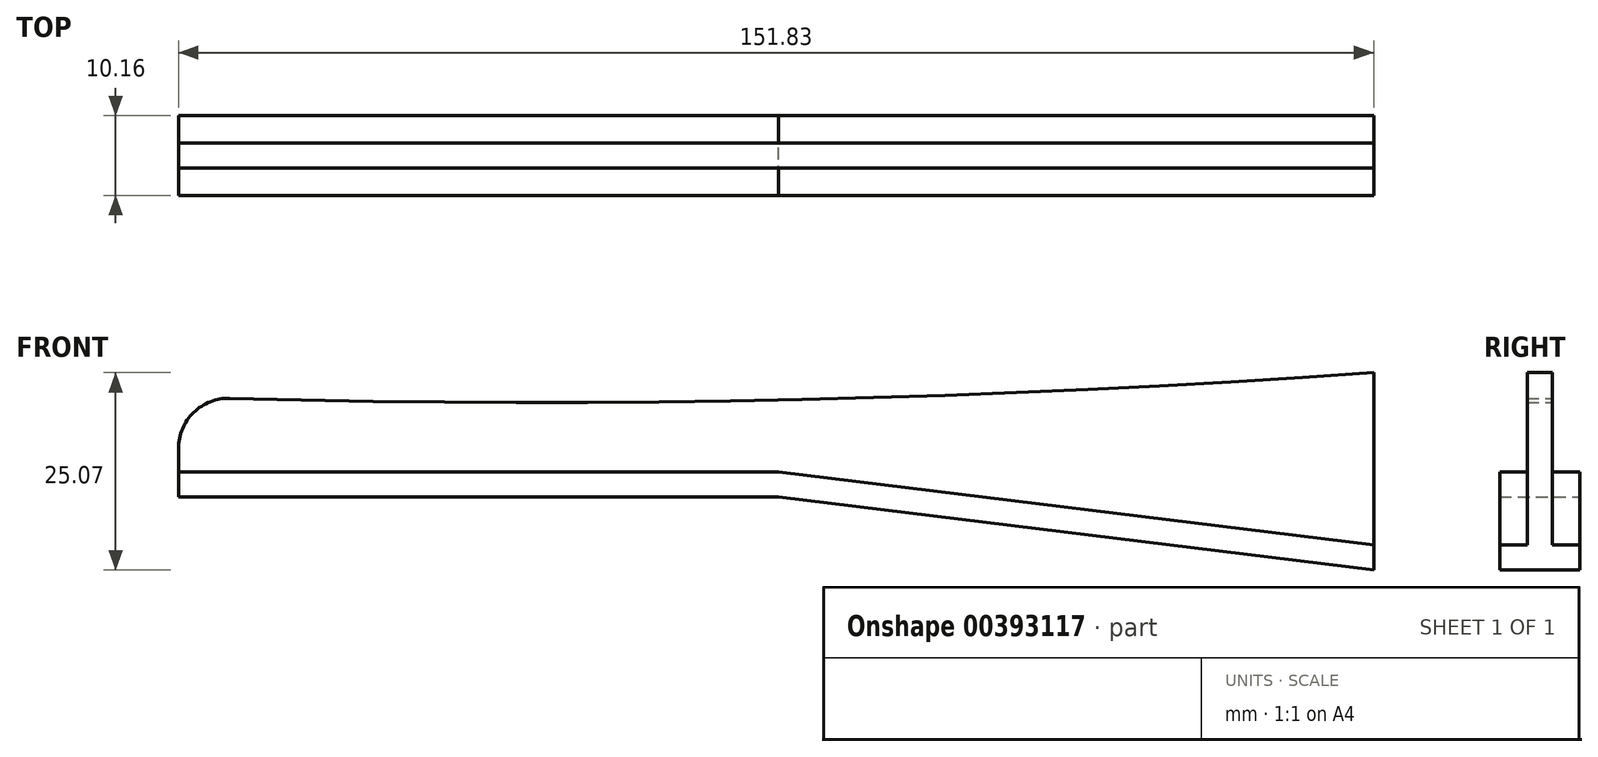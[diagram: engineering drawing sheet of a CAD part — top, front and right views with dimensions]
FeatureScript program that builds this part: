
annotation { "Feature Type Name" : "Feature", "Feature Type Description" : "" }
export const myFeature = defineFeature(function(context is Context, id is Id, definition is map)
    precondition{}
    {
        {
            var Q0;
            Q0=qCreatedBy(makeId("Front.planeOp"),FACE);
            var sketch = newSketch(context, id + "F0", { "sketchPlane" : qUnion([Q0])});
            skLineSegment(sketch, "E0.top", {"start": v(-40.64, -12.7) * mm, "end": v(35.56, -12.7) * mm});
            skLineSegment(sketch, "E0.left", {"start": v(-40.64, -6.54) * mm, "end": v(-40.64, -12.7) * mm});
            skLineSegment(sketch, "E0.right", {"start": v(35.56, -0.4) * mm, "end": v(35.56, -12.7) * mm});
            skPoint(sketch, "E0.middle", {"position": v(0, 0) * mm});
            skLineSegment(sketch, "E1", {"start": v(35.56, -12.7) * mm, "end": v(111.2, -12.7) * mm});
            skLineSegment(sketch, "E2", {"start": v(35.56, -12.7) * mm, "end": v(111.2, -21.99) * mm});
            skLineSegment(sketch, "E3", {"start": v(111.2, -21.99) * mm, "end": v(111.2, 3.08) * mm});
            skPoint(sketch, "E4", {"position": v(111.2, -12.7) * mm});
            skPoint(sketch, "E5", {"position": v(-40.64, 0) * mm});
            skPoint(sketch, "E6", {"position": v(111.2, 3.08) * mm});
            skArc(sketch, "E7", {"start": v(-34.12, -0.19) * mm, "mid": v(38.58, -0.34) * mm, "end": v(111.2, 3.08) * mm});
            skPoint(sketch, "E8", {"position": v(-40.64, -9.53) * mm});
            skPoint(sketch, "E9", {"position": v(35.56, -9.53) * mm});
            skPoint(sketch, "E9.positionSnap0", {"position": v(35.56, -6.55) * mm});
            skPoint(sketch, "E10", {"position": v(111.2, -18.81) * mm});
            skLineSegment(sketch, "E11", {"start": v(-40.64, -9.53) * mm, "end": v(35.56, -9.53) * mm});
            skLineSegment(sketch, "E12", {"start": v(35.56, -9.53) * mm, "end": v(111.2, -18.81) * mm});
            skArc(sketch, "E13.filletArc", {"start": v(-34.12, -0.19) * mm, "mid": v(-38.72, -1.99) * mm, "end": v(-40.64, -6.54) * mm});
            skSolve(sketch);
        }
        {
            var Q0;
            {var subQ0=sQuery(id+"F0.wireOp",EDGE,"E0.top");Q0=makeQuery(id+"F0.imprint","IMPRINT",FACE,{"disambiguationData":[TD([[makeQuery(id+"F0.imprint","IMPRINT",EDGE,{"derivedFrom":subQ0}),1.0]])]});}
            var Q1;
            {var subQ0=sQuery(id+"F0.wireOp",EDGE,"E2");Q1=makeQuery(id+"F0.imprint","IMPRINT",FACE,{"disambiguationData":[TD([[makeQuery(id+"F0.imprint","IMPRINT",EDGE,{"derivedFrom":subQ0}),1.0]])]});}
            var Q2;
            {var subQ0=sQuery(id+"F0.wireOp",EDGE,"E1");var subQ3=sQuery(id+"F0.wireOp",EDGE,"E12");var subQ5=makeQuery(id+"F0.imprint","INTERSECT",VERTEX,{"derivedFrom":[subQ0,subQ3]});Q2=makeQuery(id+"F0.imprint","IMPRINT",FACE,{"disambiguationData":[TD([[makeQuery(id+"F0.imprint","IMPRINT",EDGE,{"disambiguationData":[TD([[subQ5,1.0]])],"derivedFrom":subQ3}),-1.0]])]});}
            extrude(context, id + "F1", {"entities" : qUnion([Q0, Q1, Q2]), "endBound" : BoundingType.SYMMETRIC, "depth" : 10.16 * mm});
        }
        {
            var Q0;
            {var subQ3=sQuery(id+"F0.wireOp",EDGE,"E11");Q0=makeQuery(id+"F0.imprint","IMPRINT",FACE,{"disambiguationData":[TD([[makeQuery(id+"F0.imprint","IMPRINT",EDGE,{"derivedFrom":subQ3}),1.0]])]});}
            var Q1;
            {var subQ3=sQuery(id+"F0.wireOp",EDGE,"E3");var subQ5=sQuery(id+"F0.wireOp",EDGE,"E1");var subQ6=makeQuery(id+"F0.imprint","INTERSECT",VERTEX,{"derivedFrom":[subQ5,subQ3]});Q1=makeQuery(id+"F0.imprint","IMPRINT",FACE,{"disambiguationData":[TD([[makeQuery(id+"F0.imprint","IMPRINT",EDGE,{"disambiguationData":[TD([[subQ6,1.0]])],"derivedFrom":subQ5}),1.0]])]});}
            var Q2;
            {var subQ0=sQuery(id+"F0.wireOp",EDGE,"E3");var subQ1=sQuery(id+"F0.wireOp",EDGE,"E1");var subQ2=makeQuery(id+"F0.imprint","INTERSECT",VERTEX,{"derivedFrom":[subQ1,subQ0]});Q2=makeQuery(id+"F0.imprint","IMPRINT",FACE,{"disambiguationData":[TD([[makeQuery(id+"F0.imprint","IMPRINT",EDGE,{"disambiguationData":[TD([[subQ2,1.0]])],"derivedFrom":subQ1}),-1.0]])]});}
            extrude(context, id + "F2", {"entities" : qUnion([Q0, Q1, Q2]), "operationType" : NewBodyOperationType.ADD, "endBound" : BoundingType.SYMMETRIC, "depth" : 3.17 * mm});
        }
    });
